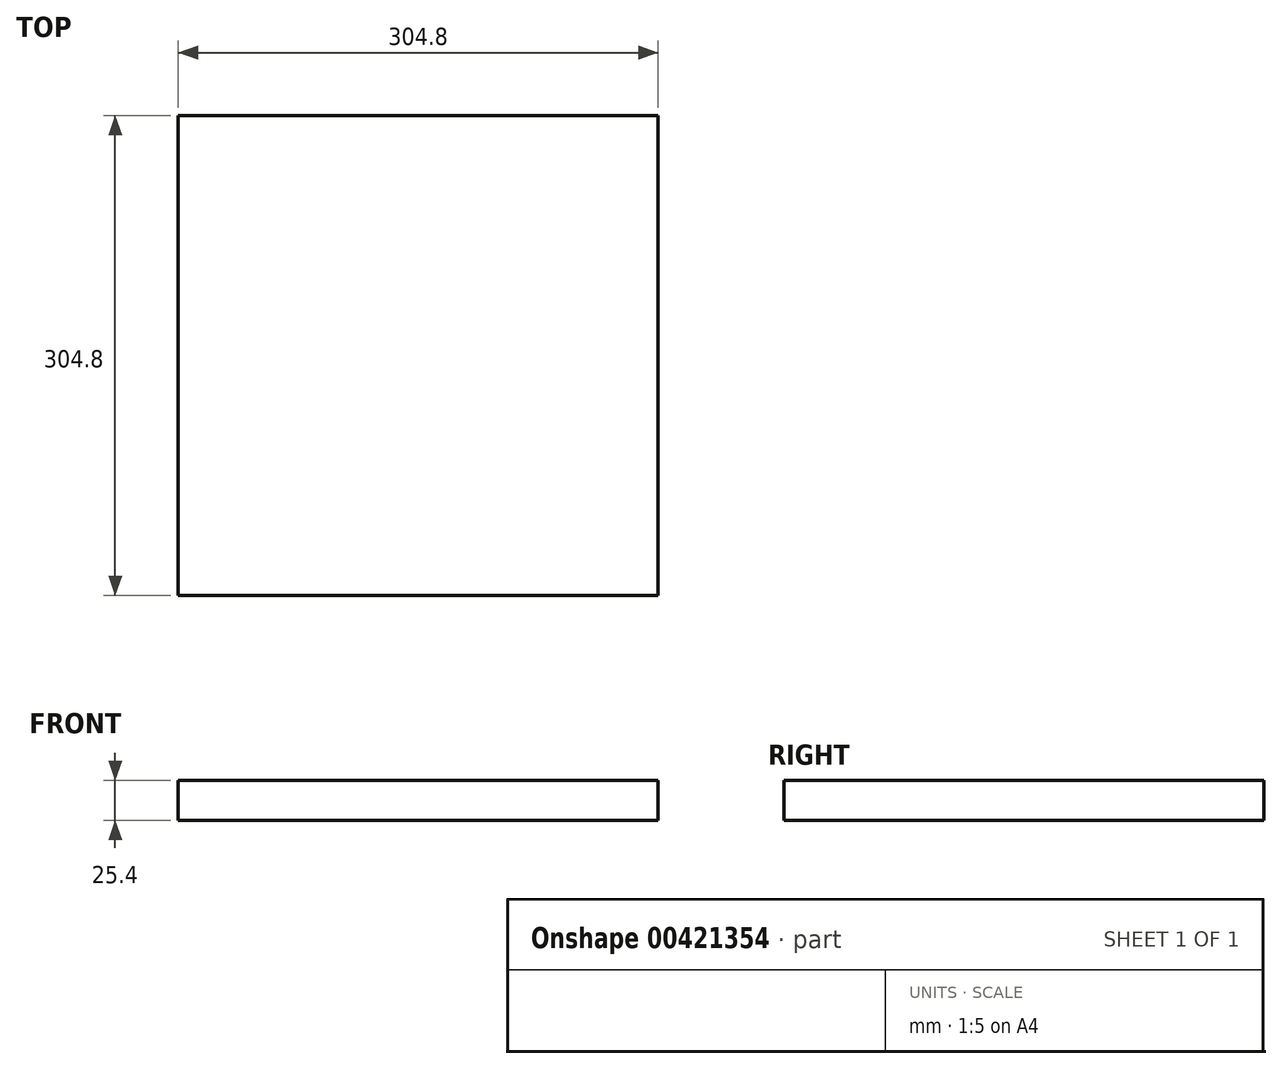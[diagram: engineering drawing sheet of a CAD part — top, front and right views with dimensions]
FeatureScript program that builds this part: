
annotation { "Feature Type Name" : "Feature", "Feature Type Description" : "" }
export const myFeature = defineFeature(function(context is Context, id is Id, definition is map)
    precondition{}
    {
        {
            var Q0;
            Q0=qCreatedBy(makeId("Top.planeOp"),FACE);
            var sketch = newSketch(context, id + "F0", { "sketchPlane" : qUnion([Q0])});
            skLineSegment(sketch, "E0.bottom", {"start": v(-143.3, 152.4) * mm, "end": v(161.5, 152.4) * mm});
            skLineSegment(sketch, "E0.top", {"start": v(-143.3, -152.4) * mm, "end": v(161.5, -152.4) * mm});
            skLineSegment(sketch, "E0.left", {"start": v(-143.3, 152.4) * mm, "end": v(-143.3, -152.4) * mm});
            skLineSegment(sketch, "E0.right", {"start": v(161.5, 152.4) * mm, "end": v(161.5, -152.4) * mm});
            skPoint(sketch, "E0.middle", {"position": v(9.1, 0) * mm});
            skSolve(sketch);
        }
        {
            var Q0;
            Q0 = qSketchRegion(id + "F0", true);
            extrude(context, id + "F1", {"entities" : qUnion([Q0]), "depth" : 25.4 * mm, "offsetDistance" : 25.4 * mm});
        }
    });
